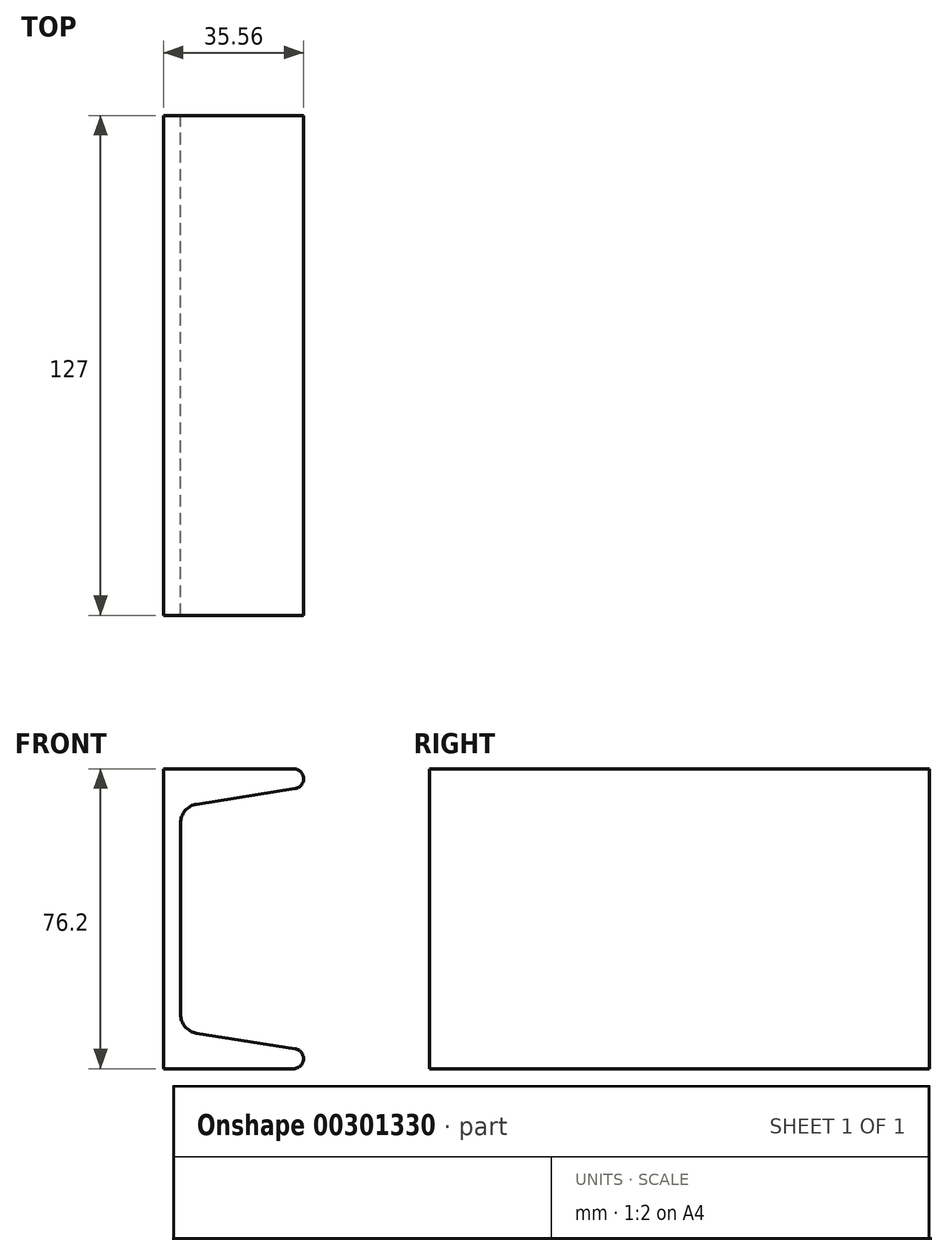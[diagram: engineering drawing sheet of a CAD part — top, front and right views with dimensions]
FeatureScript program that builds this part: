
annotation { "Feature Type Name" : "Feature", "Feature Type Description" : "" }
export const myFeature = defineFeature(function(context is Context, id is Id, definition is map)
    precondition{}
    {
        {
            var Q0;
            Q0=qCreatedBy(makeId("Front.planeOp"),FACE);
            var sketch = newSketch(context, id + "F0", { "sketchPlane" : qUnion([Q0])});
            skLineSegment(sketch, "E0", {"start": v(-72.9, 38.1) * mm, "end": v(-72.9, 0) * mm});
            skLineSegment(sketch, "E1", {"start": v(-72.9, 38.1) * mm, "end": v(-39.87, 38.1) * mm});
            skLineSegment(sketch, "E2", {"start": v(-39.48, 33.05) * mm, "end": v(-64.48, 29.1) * mm});
            skLineSegment(sketch, "E3", {"start": v(-68.58, 24.3) * mm, "end": v(-68.58, 0) * mm});
            skPoint(sketch, "E4.visualSharp", {"position": v(-7.6, 38.1) * mm});
            skArc(sketch, "E4.filletArc", {"start": v(-39.48, 33.05) * mm, "mid": v(-37.34, 35.76) * mm, "end": v(-39.87, 38.1) * mm});
            skPoint(sketch, "E5.visualSharp", {"position": v(-68.58, 28.44) * mm});
            skArc(sketch, "E5.filletArc", {"start": v(-64.48, 29.1) * mm, "mid": v(-67.41, 27.45) * mm, "end": v(-68.58, 24.3) * mm});
            skArc(sketch, "E6.MirrorCS", {"start": v(-64.48, -29.1) * mm, "mid": v(-67.41, -27.45) * mm, "end": v(-68.58, -24.3) * mm});
            skArc(sketch, "E7.MirrorCS", {"start": v(-39.48, -33.05) * mm, "mid": v(-37.34, -35.76) * mm, "end": v(-39.87, -38.1) * mm});
            skPoint(sketch, "E8.MirrorP", {"position": v(-7.6, -38.1) * mm});
            skLineSegment(sketch, "E9.MirrorCS", {"start": v(-68.58, -24.3) * mm, "end": v(-68.58, 0) * mm});
            skPoint(sketch, "E10.MirrorP", {"position": v(-68.58, -28.44) * mm});
            skLineSegment(sketch, "E11.MirrorCS", {"start": v(-39.48, -33.05) * mm, "end": v(-64.48, -29.1) * mm});
            skLineSegment(sketch, "E12.MirrorCS", {"start": v(-72.9, -38.1) * mm, "end": v(-72.9, 0) * mm});
            skLineSegment(sketch, "E13.MirrorCS", {"start": v(-72.9, -38.1) * mm, "end": v(-39.87, -38.1) * mm});
            skSolve(sketch);
        }
        {
            var Q0;
            Q0 = qSketchRegion(id + "F0", true);
            extrude(context, id + "F1", {"entities" : qUnion([Q0]), "endBound" : BoundingType.SYMMETRIC, "depth" : 127 * mm});
        }
    });
